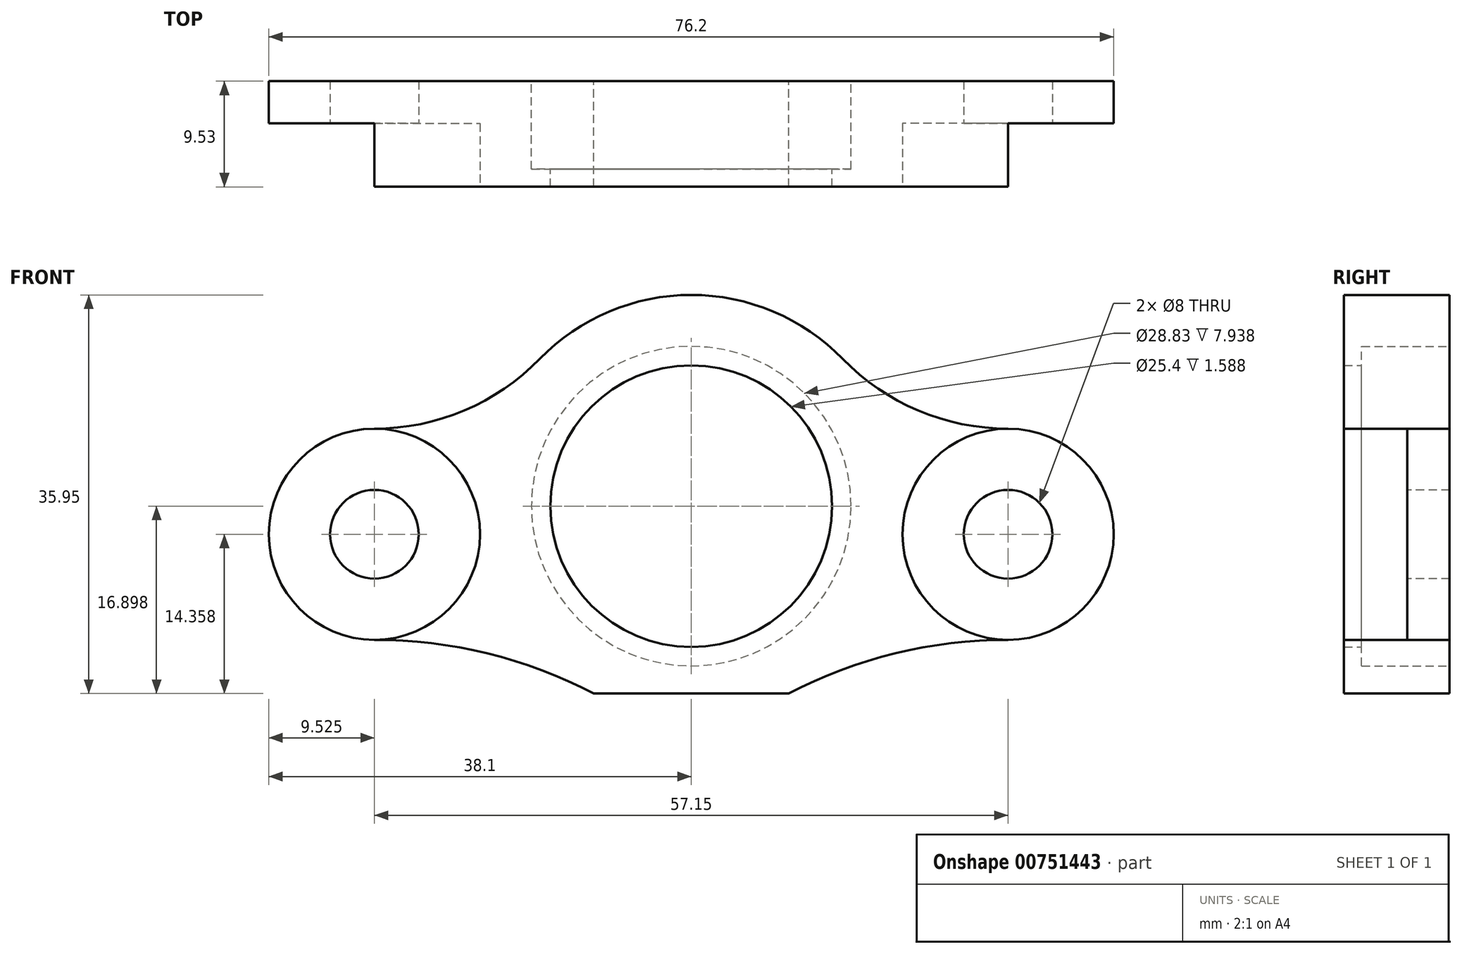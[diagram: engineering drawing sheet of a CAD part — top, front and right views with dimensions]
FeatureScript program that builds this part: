
annotation { "Feature Type Name" : "Feature", "Feature Type Description" : "" }
export const myFeature = defineFeature(function(context is Context, id is Id, definition is map)
    precondition{}
    {
        {
            var Q0;
            Q0=qCreatedBy(makeId("Front.planeOp"),FACE);
            var sketch = newSketch(context, id + "F0", { "sketchPlane" : qUnion([Q0])});
            skLineSegment(sketch, "E0.bottom", {"start": v(-38.1, 15.06) * mm, "end": v(38.1, 15.06) * mm, "construction": true});
            skLineSegment(sketch, "E0.top", {"start": v(-38.1, -15.06) * mm, "end": v(38.1, -15.06) * mm, "construction": true});
            skLineSegment(sketch, "E0.left", {"start": v(-38.1, 15.06) * mm, "end": v(-38.1, -15.06) * mm, "construction": true});
            skLineSegment(sketch, "E0.right", {"start": v(38.1, 15.06) * mm, "end": v(38.1, -15.06) * mm, "construction": true});
            skPoint(sketch, "E1", {"position": v(-38.1, 0) * mm});
            skPoint(sketch, "E2", {"position": v(0, 15.06) * mm});
            skCircle(sketch, "E3", {"center": v(-28.57, 1.45) * mm, "radius": 4.76 * mm, "construction": true});
            skArc(sketch, "E4", {"start": v(-11.11, 6.21) * mm, "mid": v(-15.88, 1.45) * mm, "end": v(-11.11, -3.31) * mm, "construction": true});
            skArc(sketch, "E5", {"start": v(-7.94, -3.31) * mm, "mid": v(-3.17, 1.45) * mm, "end": v(-7.94, 6.21) * mm, "construction": true});
            skLineSegment(sketch, "E6", {"start": v(-11.11, 6.21) * mm, "end": v(-7.94, 6.21) * mm, "construction": true});
            skLineSegment(sketch, "E7", {"start": v(-11.11, -3.31) * mm, "end": v(-7.94, -3.31) * mm, "construction": true});
            skArc(sketch, "E8", {"start": v(7.94, 6.21) * mm, "mid": v(3.18, 1.45) * mm, "end": v(7.94, -3.31) * mm, "construction": true});
            skArc(sketch, "E9", {"start": v(11.11, -3.31) * mm, "mid": v(15.88, 1.45) * mm, "end": v(11.11, 6.21) * mm, "construction": true});
            skLineSegment(sketch, "E10", {"start": v(7.94, 6.21) * mm, "end": v(11.11, 6.21) * mm, "construction": true});
            skLineSegment(sketch, "E11", {"start": v(7.94, -3.31) * mm, "end": v(11.11, -3.31) * mm, "construction": true});
            skCircle(sketch, "E12", {"center": v(28.57, 1.45) * mm, "radius": 4.76 * mm, "construction": true});
            skLineSegment(sketch, "E13.top", {"start": v(-38.1, -13.7) * mm, "end": v(38.1, -13.7) * mm, "construction": true});
            skLineSegment(sketch, "E13.left", {"start": v(-38.1, -15.06) * mm, "end": v(-38.1, -13.7) * mm, "construction": true});
            skLineSegment(sketch, "E13.right", {"start": v(38.1, -15.06) * mm, "end": v(38.1, -13.7) * mm, "construction": true});
            skCircle(sketch, "E14", {"center": v(0, 3.99) * mm, "radius": 6.35 * mm, "construction": true});
            skCircle(sketch, "E15", {"center": v(0, 3.99) * mm, "radius": 14.29 * mm, "construction": true});
            skCircle(sketch, "E16", {"center": v(0, 3.99) * mm, "radius": 50.8 * mm, "construction": true});
            skSolve(sketch);
        }
        {
            var Q0;
            Q0=qCreatedBy(makeId("Front.planeOp"),FACE);
            var sketch = newSketch(context, id + "F1", { "sketchPlane" : qUnion([Q0])});
            skCircle(sketch, "E17", {"center": v(0, 3.99) * mm, "radius": 14.41 * mm});
            skArc(sketch, "E18", {"start": v(-28.57, 10.97) * mm, "mid": v(-38.1, 1.45) * mm, "end": v(-28.58, -8.08) * mm});
            skArc(sketch, "E19", {"start": v(28.57, -8.08) * mm, "mid": v(38.1, 1.45) * mm, "end": v(28.57, 10.97) * mm});
            skArc(sketch, "E20", {"start": v(-8.79, -12.91) * mm, "mid": v(0, -15.06) * mm, "end": v(8.79, -12.91) * mm});
            skLineSegment(sketch, "E21", {"start": v(-28.57, -8.08) * mm, "end": v(-28.57, -8.08) * mm});
            skLineSegment(sketch, "E22", {"start": v(-28.57, 10.97) * mm, "end": v(-28.57, 10.97) * mm});
            skLineSegment(sketch, "E23", {"start": v(28.57, 10.97) * mm, "end": v(28.57, 10.97) * mm});
            skLineSegment(sketch, "E24", {"start": v(28.57, -8.08) * mm, "end": v(28.57, -8.08) * mm});
            skArc(sketch, "E25", {"start": v(-28.57, 10.97) * mm, "mid": v(-20.48, 12.61) * mm, "end": v(-13.65, 17.27) * mm});
            skArc(sketch, "E26", {"start": v(-8.79, -12.91) * mm, "mid": v(-18.4, -9.3) * mm, "end": v(-28.58, -8.08) * mm});
            skArc(sketch, "E27", {"start": v(28.57, -8.08) * mm, "mid": v(18.4, -9.3) * mm, "end": v(8.79, -12.91) * mm});
            skArc(sketch, "E28", {"start": v(13.65, 17.27) * mm, "mid": v(20.48, 12.61) * mm, "end": v(28.57, 10.97) * mm});
            skArc(sketch, "E29.trimOffspring", {"start": v(13.65, 17.27) * mm, "mid": v(0, 23.04) * mm, "end": v(-13.65, 17.27) * mm});
            skLineSegment(sketch, "E30", {"start": v(-8.79, -12.91) * mm, "end": v(8.79, -12.91) * mm});
            skSolve(sketch);
        }
        {
            var Q0;
            Q0=makeQuery(id+"F1.imprint","IMPRINT",FACE,{"disambiguationData":[TD([[makeQuery(id+"F1.imprint","IMPRINT",EDGE,{"derivedFrom":sQuery(id+"F1.wireOp",EDGE,"E17")}),-1.0]])]});
            extrude(context, id + "F2", {"entities" : qUnion([Q0]), "depth" : 7.94 * mm, "offsetDistance" : 25.4 * mm});
        }
        {
            var Q0;
            Q0=makeQuery(id+"F2.opExtrude","CAP_FACE",FACE,{"disambiguationData":[OSD([sQuery(id+"F1.wireOp",EDGE,"E17"),sQuery(id+"F1.wireOp",EDGE,"E18"),sQuery(id+"F1.wireOp",EDGE,"E19"),sQuery(id+"F1.wireOp",EDGE,"E20"),sQuery(id+"F1.wireOp",EDGE,"E25"),sQuery(id+"F1.wireOp",EDGE,"E26"),sQuery(id+"F1.wireOp",EDGE,"E27"),sQuery(id+"F1.wireOp",EDGE,"E28"),sQuery(id+"F1.wireOp",EDGE,"E29.trimOffspring")])],"isStart":false});
            var sketch = newSketch(context, id + "F3", { "sketchPlane" : qUnion([Q0])});
            skCircle(sketch, "E31", {"center": v(0, 3.99) * mm, "radius": 14.41 * mm});
            skCircle(sketch, "E32", {"center": v(0, 3.99) * mm, "radius": 12.7 * mm});
            skSolve(sketch);
        }
        {
            var Q0;
            Q0=makeQuery(id+"F3.imprint","IMPRINT",FACE,{"disambiguationData":[TD([[makeQuery(id+"F3.imprint","IMPRINT",EDGE,{"derivedFrom":sQuery(id+"F3.wireOp",EDGE,"E31")}),-1.0]])]});
            var Q1;
            Q1=makeQuery(id+"F3.imprint","IMPRINT",FACE,{"disambiguationData":[TD([[makeQuery(id+"F3.imprint","IMPRINT",EDGE,{"derivedFrom":sQuery(id+"F3.wireOp",EDGE,"E31")}),1.0]])]});
            extrude(context, id + "F4", {"entities" : qUnion([Q0, Q1]), "operationType" : NewBodyOperationType.ADD, "depth" : 1.59 * mm, "offsetDistance" : 25.4 * mm});
        }
        {
            var Q0;
            Q0=makeQuery(id+"F4.opExtrude","CAP_FACE",FACE,{"disambiguationData":[OSD([sQuery(id+"F1.wireOp",EDGE,"E18"),sQuery(id+"F1.wireOp",EDGE,"E19"),sQuery(id+"F1.wireOp",EDGE,"E20"),sQuery(id+"F1.wireOp",EDGE,"E25"),sQuery(id+"F1.wireOp",EDGE,"E26"),sQuery(id+"F1.wireOp",EDGE,"E27"),sQuery(id+"F1.wireOp",EDGE,"E28"),sQuery(id+"F1.wireOp",EDGE,"E29.trimOffspring"),sQuery(id+"F3.wireOp",EDGE,"E32")])],"isStart":false});
            var sketch = newSketch(context, id + "F5", { "sketchPlane" : qUnion([Q0])});
            skCircle(sketch, "E33", {"center": v(-28.57, 1.45) * mm, "radius": 4 * mm});
            skCircle(sketch, "E34", {"center": v(28.57, 1.45) * mm, "radius": 4 * mm});
            skCircle(sketch, "E35", {"center": v(-28.57, 1.45) * mm, "radius": 9.53 * mm});
            skCircle(sketch, "E36", {"center": v(28.57, 1.45) * mm, "radius": 9.53 * mm});
            skSolve(sketch);
        }
        {
            var Q0;
            Q0=makeQuery(id+"F5.imprint","IMPRINT",FACE,{"disambiguationData":[TD([[makeQuery(id+"F5.imprint","IMPRINT",EDGE,{"derivedFrom":sQuery(id+"F5.wireOp",EDGE,"E33")}),-1.0]])]});
            var Q1;
            Q1=makeQuery(id+"F5.imprint","IMPRINT",FACE,{"disambiguationData":[TD([[makeQuery(id+"F5.imprint","IMPRINT",EDGE,{"derivedFrom":sQuery(id+"F5.wireOp",EDGE,"E34")}),-1.0]])]});
            extrude(context, id + "F6", {"entities" : qUnion([Q0, Q1]), "operationType" : NewBodyOperationType.REMOVE, "oppositeDirection" : true, "depth" : 5.7 * mm, "offsetDistance" : 25.4 * mm});
        }
        {
            var Q0;
            Q0=makeQuery(id+"F6.boolean.opBoolean","SPLIT",FACE,{"disambiguationData":[TD([makeQuery(id+"F6.opExtrude","SWEPT_FACE",FACE,{"disambiguationData":[OSD([sQuery(id+"F5.wireOp",EDGE,"E33")])]})])],"derivedFrom":makeQuery(id+"F4.opExtrude","CAP_FACE",FACE,{"disambiguationData":[OSD([sQuery(id+"F1.wireOp",EDGE,"E18"),sQuery(id+"F1.wireOp",EDGE,"E19"),sQuery(id+"F1.wireOp",EDGE,"E20"),sQuery(id+"F1.wireOp",EDGE,"E25"),sQuery(id+"F1.wireOp",EDGE,"E26"),sQuery(id+"F1.wireOp",EDGE,"E27"),sQuery(id+"F1.wireOp",EDGE,"E28"),sQuery(id+"F1.wireOp",EDGE,"E29.trimOffspring"),sQuery(id+"F3.wireOp",EDGE,"E32")])],"isStart":false})});
            var Q1;
            Q1=makeQuery(id+"F6.boolean.opBoolean","SPLIT",FACE,{"disambiguationData":[TD([makeQuery(id+"F6.opExtrude","SWEPT_FACE",FACE,{"disambiguationData":[OSD([sQuery(id+"F5.wireOp",EDGE,"E34")])]})])],"derivedFrom":makeQuery(id+"F4.opExtrude","CAP_FACE",FACE,{"disambiguationData":[OSD([sQuery(id+"F1.wireOp",EDGE,"E18"),sQuery(id+"F1.wireOp",EDGE,"E19"),sQuery(id+"F1.wireOp",EDGE,"E20"),sQuery(id+"F1.wireOp",EDGE,"E25"),sQuery(id+"F1.wireOp",EDGE,"E26"),sQuery(id+"F1.wireOp",EDGE,"E27"),sQuery(id+"F1.wireOp",EDGE,"E28"),sQuery(id+"F1.wireOp",EDGE,"E29.trimOffspring"),sQuery(id+"F3.wireOp",EDGE,"E32")])],"isStart":false})});
            extrude(context, id + "F7", {"entities" : qUnion([Q0, Q1]), "operationType" : NewBodyOperationType.REMOVE, "endBound" : BoundingType.THROUGH_ALL, "oppositeDirection" : true, "depth" : 25.4 * mm, "offsetDistance" : 25.4 * mm});
        }
    });
